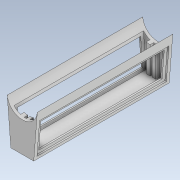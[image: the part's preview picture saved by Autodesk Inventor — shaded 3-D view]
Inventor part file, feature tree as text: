
AUTODESK INVENTOR PART (.ipt)
format: ipt  version: 2021 (Build 250183000, 183)  size: 176,640 bytes
history: native  units: in
note: dims shown in document units (in); Inventor stores cm internally (conversion verified against a paired STEP export)
features: extrude x6, sketch x6, mirror x2, projected_geometry x2, shell x1, plane x1
ambient origin geometry x8: Origin, YZ Plane, XZ Plane, XY Plane, X Axis, Y Axis, Z Axis, Center Point
bodies: Solid1 (feature_tree)
feature tree (18):
  extrude  "Extrusion1"  Depth=1.5in
  shell  "Shell1"  Thickness=0.3804in
  sketch  "Sketch2"  dims[d3=0.3804in d4=4.5in d5=0.0in]
  extrude  "Extrusion2"  Depth=4.5in TaperAngle=0.0deg
  extrude  "Extrusion3"  Depth=0.05in TaperAngle=0.0deg
  mirror  "Mirror1"
  extrude  "Extrusion4"  Depth=0.05in TaperAngle=0.0deg
  plane  "Work Plane1"
  mirror  "Mirror2"
  extrude  "Extrusion6"  Depth=0.12in
  extrude  "Extrusion7"  Depth=0.12in TaperAngle=0.0deg
  sketch  "Sketch1"  dims[d0=1.0in d1=1.5in d2=0.3804in]
  projected_geometry  "Projected Loop1"
  sketch  "Sketch3"  dims[d6=0.1in d7=0.05in d8=0.0in]
  projected_geometry  "Projected Loop2"
  sketch  "Sketch4"  dims[d9=0.1in d10=0.05in d11=0.0in]
  sketch  "Sketch6"  dims[d12=0.035in d13=0.12in]
  sketch  "Sketch7"  dims[d14=0.12in d15=1.05in d16=0.0in d19=-2.25in d20=12.0in d21=0.0in d22=0.25in d23=0.0in]
